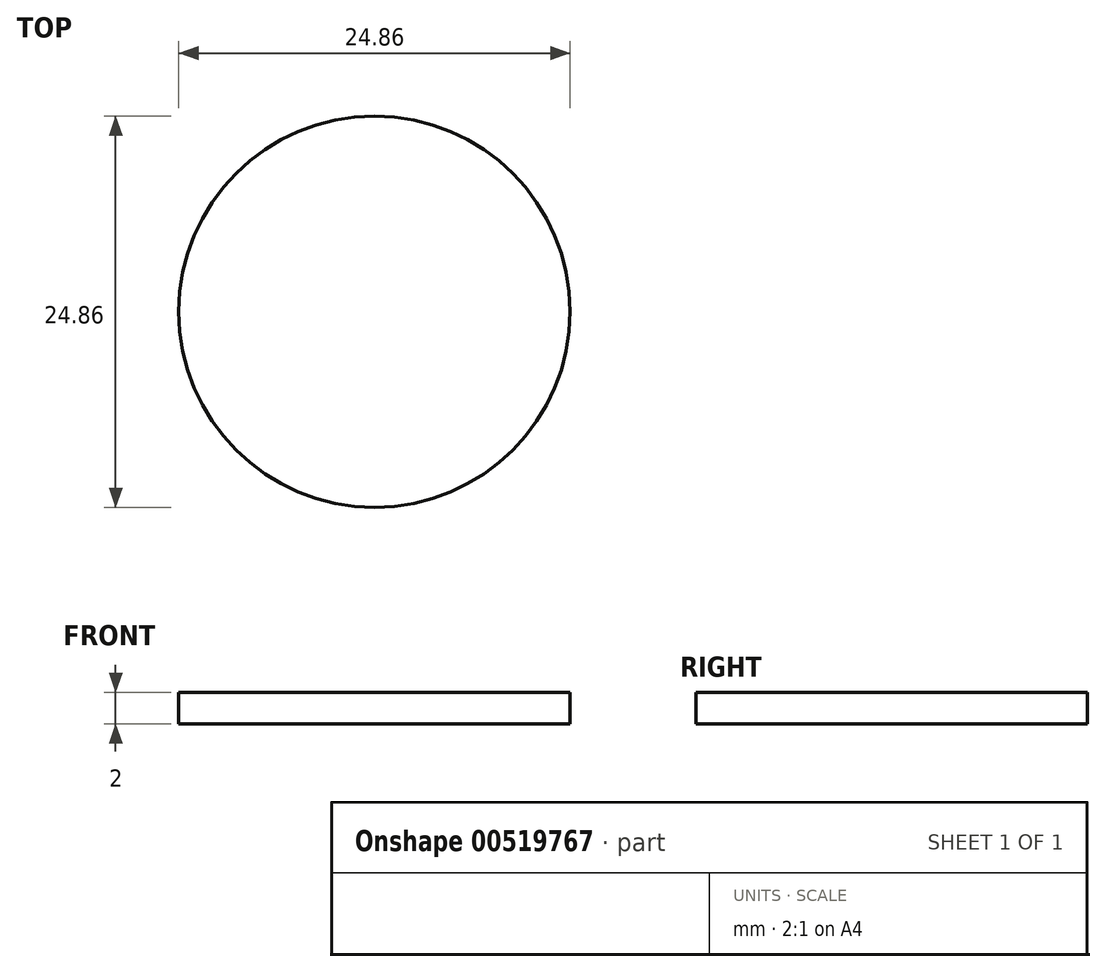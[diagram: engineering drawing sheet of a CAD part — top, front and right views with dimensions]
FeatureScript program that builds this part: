
annotation { "Feature Type Name" : "Feature", "Feature Type Description" : "" }
export const myFeature = defineFeature(function(context is Context, id is Id, definition is map)
    precondition{}
    {
        {
            var Q0;
            Q0=qCreatedBy(makeId("Top.planeOp"),FACE);
            var sketch = newSketch(context, id + "F0", { "sketchPlane" : qUnion([Q0])});
            skCircle(sketch, "E0", {"center": v(0, 0) * mm, "radius": 12.43 * mm});
            skSolve(sketch);
        }
        {
            var Q0;
            Q0=makeQuery(id+"F0.imprint","IMPRINT",FACE,{"disambiguationData":[TD([[makeQuery(id+"F0.imprint","IMPRINT",EDGE,{"derivedFrom":sQuery(id+"F0.wireOp",EDGE,"E0")}),1.0]])]});
            extrude(context, id + "F1", {"entities" : qUnion([Q0]), "depth" : 2 * mm, "offsetDistance" : 25 * mm});
        }
    });
